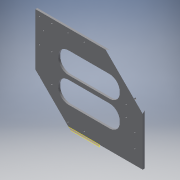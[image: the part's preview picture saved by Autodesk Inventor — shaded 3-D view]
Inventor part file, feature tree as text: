
AUTODESK INVENTOR PART (.ipt)
format: ipt  version: 2016 (Build 200138000, 138)  size: 209,408 bytes
history: native  units: in
note: dims shown in document units (in); Inventor stores cm internally (conversion verified against a paired STEP export)
features: extrude x6, sketch x6, projected_geometry x3, plane x1, fillet x1, reference x1
ambient origin geometry x8: Origin, YZ Plane, XZ Plane, XY Plane, X Axis, Y Axis, Z Axis, Center Point
bodies: Solid1 (feature_tree)
feature tree (18):
  plane  "Work Plane1"
  extrude  "Extrusion1"  Depth=0.24in TaperAngle=0.0deg
  extrude  "Extrusion2"  Depth=2.0in
  extrude  "Extrusion3"  Depth=0.5in
  extrude  "Extrusion4"  Depth=0.175in
  extrude  "Extrusion5"  Depth=1.5in
  extrude  "Extrusion6"  Depth=1.25in TaperAngle=0.0deg
  fillet  "Fillet1"  Radius=0.175in
  sketch  "Sketch1"  dims[d0=13.25in d1=0.24in d2=0.0in]
  sketch  "Sketch2"  dims[d3=2.0in d4=2.0in]
  projected_geometry  "Projected Loop1"
  sketch  "Sketch3"  dims[d5=2.0in d6=0.5in]
  projected_geometry  "Projected Loop2"
  sketch  "Sketch4"  dims[d7=0.175in d8=0.175in]
  projected_geometry  "Projected Loop3"
  sketch  "Sketch5"  dims[d9=0.175in d10=1.5in]
  reference  "Reference1"
  sketch  "Sketch6"  dims[d11=0.175in d12=0.4275in d13=0.0in d20=0.175in d21=0.175in d22=0.175in d23=0.175in d24=0.175in d25=0.175in d26=0.4275in d27=0.0in d31=0.175in d32=0.175in d33=0.175in d37=0.175in d38=0.175in d39=0.4275in d40=0.0in d41=0.4275in d42=0.0in d43=0.5in d44=0.4275in d45=0.0in d46=1.25in]
